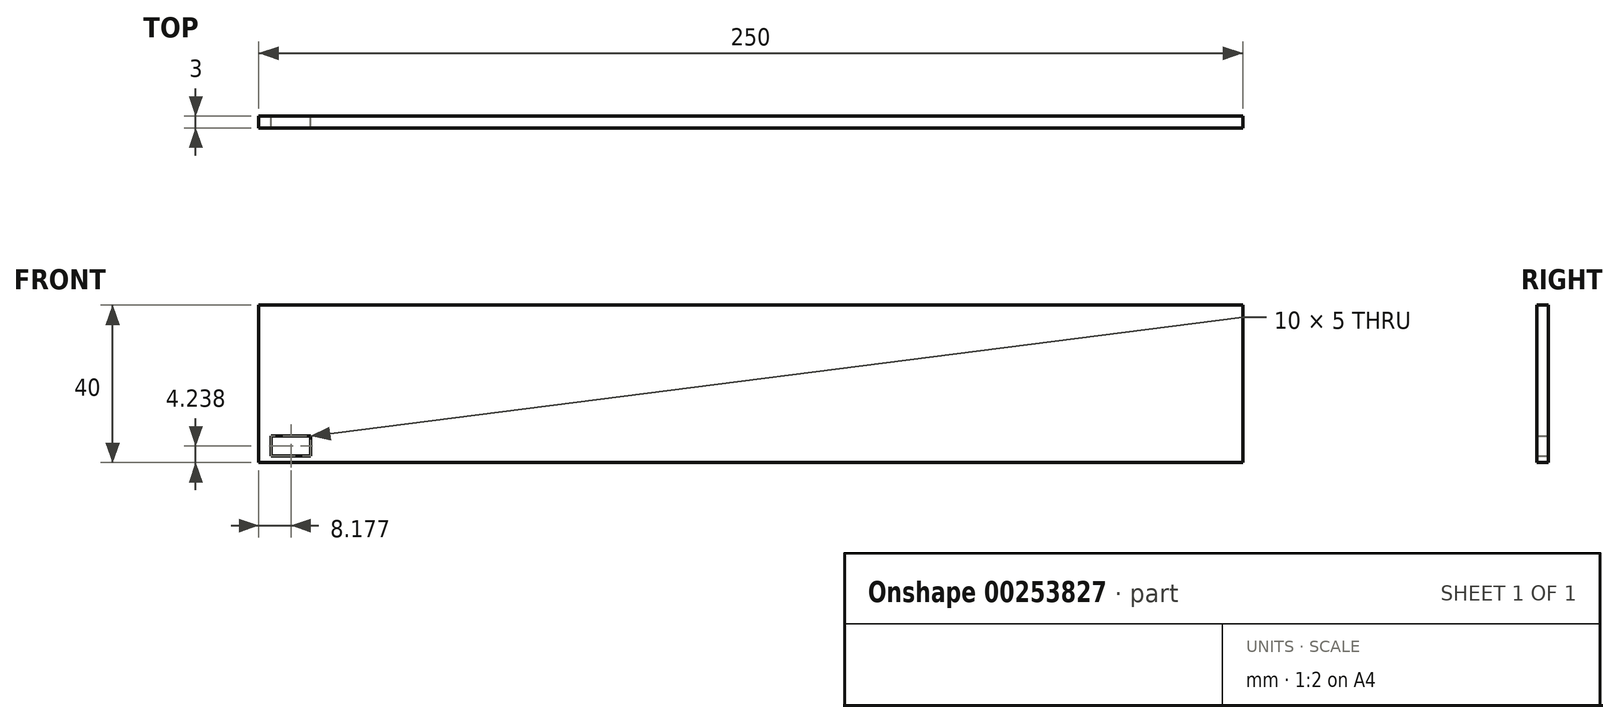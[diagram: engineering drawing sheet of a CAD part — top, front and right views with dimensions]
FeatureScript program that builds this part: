
annotation { "Feature Type Name" : "Feature", "Feature Type Description" : "" }
export const myFeature = defineFeature(function(context is Context, id is Id, definition is map)
    precondition{}
    {
        {
            var Q0;
            Q0=qCreatedBy(makeId("Front.planeOp"),FACE);
            var sketch = newSketch(context, id + "F0", { "sketchPlane" : qUnion([Q0])});
            skLineSegment(sketch, "E0", {"start": v(-125, 20) * mm, "end": v(125, 20) * mm});
            skLineSegment(sketch, "E1", {"start": v(125, 20) * mm, "end": v(125, -20) * mm});
            skLineSegment(sketch, "E2", {"start": v(125, -20) * mm, "end": v(-125, -20) * mm});
            skLineSegment(sketch, "E3", {"start": v(-125, -20) * mm, "end": v(-125, 20) * mm});
            skLineSegment(sketch, "E4", {"start": v(-111.82, -18.26) * mm, "end": v(-121.82, -18.26) * mm});
            skLineSegment(sketch, "E5", {"start": v(-121.82, -18.26) * mm, "end": v(-121.82, -13.26) * mm});
            skLineSegment(sketch, "E6", {"start": v(-121.82, -13.26) * mm, "end": v(-111.82, -13.26) * mm});
            skLineSegment(sketch, "E7", {"start": v(-111.82, -13.26) * mm, "end": v(-111.82, -18.26) * mm});
            skSolve(sketch);
        }
        {
            var Q0;
            Q0 = qSketchRegion(id + "F0", true);
            extrude(context, id + "F1", {"entities" : qUnion([Q0]), "depth" : 3 * mm});
        }
    });
